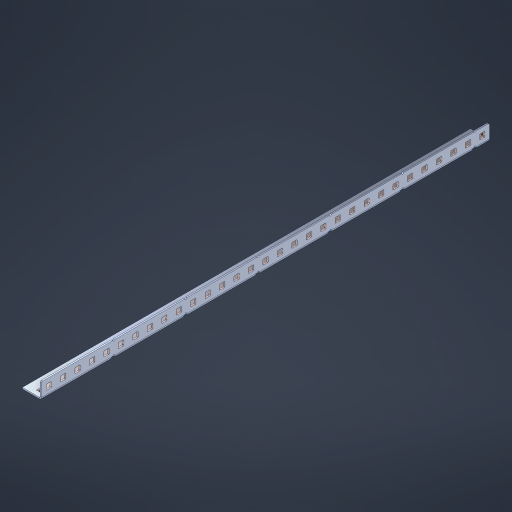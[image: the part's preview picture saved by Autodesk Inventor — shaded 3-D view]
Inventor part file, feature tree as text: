
AUTODESK INVENTOR PART (.ipt)
format: ipt  version: 2023 (Build 270158000, 158)  size: 975,872 bytes
history: native  units: in
note: dims shown in document units (in); Inventor stores cm internally (conversion verified against a paired STEP export)
features: other x67, extrude x61, sheet_metal_op x10, sketch x8, mirror x1, pattern_linear x1, chamfer x1
ambient origin geometry x8: Origin, YZ Plane, XZ Plane, XY Plane, X Axis, Y Axis, Z Axis, Center Point
bodies: Solid1 (feature_tree), Body (feature_tree)
feature tree (149):
  other  "Flange Pattern Plane"
  sheet_metal_op  "Flange Pattern"
  sheet_metal_op  "Body Pattern"
  other  "Arc Length"
  mirror  "Notch Mirror"
  pattern_linear  "Notch Pattern"  Spacing1=0.1875in  [1 undecoded]
  chamfer  "End Chamfer"
  extrude  "Half Cut"  Depth=0.0469in
  sketch  "Sketch1"  dims[d0=2.5in]
  other  "Plate1"
  sketch  "Sketch2"  dims[d1=15.5in]
  other  "Plate2"
  sheet_metal_op  "Bend1"
  sheet_metal_op  "Corner1"
  sketch  "Sketch3"  dims[d2=0.0469in]
  other  "Flange Pattern Sketch"
  sketch  "Sketch7"  dims[d3=0.0469in]
  other  "Srf1"
  other  "Srf2"
  sketch  "Sketch8"  dims[d4=0.0234in]
  sketch  "Sketch9"  dims[d5=0.0938in]
  other  "Srf91"
  sheet_metal_op  "Body Pattern Sketch"
  other  "Srf92"
  sketch  "Sketch13"  dims[d6=0.0469in]
  sketch  "Sketch14"  dims[d7=0.5in d8=90.0deg d9=0.0312in d10=0.1875in d11=0.0469in d12=0.0469in d16=0.182in d17=0.02in d18=0.0469in d19=0.0in d20=0.25in d21=0.25in d46=0.172in d47=1.0in d48=0.0in d49=0.182in d50=0.02in d51=0.25in d52=0.25in d53=0.0469in d54=0.0in d55=0.172in d56=1.0in d57=0.0in d60=12.2047in d62=0.5in d63=0.3937in d65=0.5in d85=0.1227in d86=0.1659in d88=0.04in d89=0.0469in d90=0.0in d91=0.04in d92=0.0491in d95=2.5in d96=0.04in d97=0.25in d98=45.0deg d101=0.0in d102=2.497in d131=0.5in d132=12.2047in d134=0.5in d139=0.5in]
  other  "Srf856"
  other  "Srf1310"
  other  "Srf1311"
  other  "Srf1312"
  other  "Srf1376"
  other  "Srf1377"
  other  "Srf1728"
  other  "Srf1755"
  other  "Srf1878"
  other  "Srf1879"
  other  "Srf1880"
  other  "Srf1881"
  other  "Srf1882"
  other  "Srf1883"
  other  "Srf1884"
  other  "Srf1885"
  other  "Srf1886"
  other  "Srf1887"
  other  "Srf1888"
  other  "Srf1889"
  other  "Srf1890"
  other  "Srf1891"
  other  "Srf1892"
  other  "Srf1893"
  other  "Srf1894"
  other  "Srf1895"
  other  "Srf1896"
  other  "Srf1897"
  other  "Srf1898"
  other  "Srf1899"
  other  "Srf1900"
  other  "Srf1901"
  other  "Srf1902"
  other  "Srf1942"
  other  "Srf1943"
  other  "Srf1944"
  other  "Srf1945"
  other  "Srf1946"
  other  "Srf1947"
  other  "Srf1948"
  other  "Srf1949"
  other  "Srf1950"
  other  "Srf1951"
  other  "Srf1952"
  other  "Srf1953"
  other  "Srf1954"
  other  "Srf1955"
  other  "Srf1956"
  other  "Srf1957"
  other  "Srf1958"
  other  "Srf1959"
  other  "Srf1960"
  other  "Srf1961"
  other  "Srf1962"
  other  "Srf1963"
  other  "Srf1964"
  other  "Srf1965"
  other  "Srf1966"
  sheet_metal_op  "Flange Stamp"
  sheet_metal_op  "Flange Circle"
  sheet_metal_op  "Body Stamp"
  sheet_metal_op  "Body Circle"
  sheet_metal_op  "Notch"
  extrude  "ExtrusionSrf2"  Depth=0.0469in
  extrude  "ExtrusionSrf92"  Depth=0.5in
  extrude  "ExtrusionSrf856"  Depth=0.02in
  extrude  "ExtrusionSrf1310"  Depth=0.0469in
  extrude  "ExtrusionSrf1311"  TaperAngle=0.0deg  [1 undecoded]
  extrude  "ExtrusionSrf1312"  Depth=0.5in
  extrude  "ExtrusionSrf1376"  Depth=0.5in
  extrude  "ExtrusionSrf1377"  Depth=0.5in
  extrude  "ExtrusionSrf1728"  Depth=0.5in TaperAngle=0.0deg
  extrude  "ExtrusionSrf1755"  Depth=0.5in
  extrude  "ExtrusionSrf1878"  Depth=0.02in
  extrude  "ExtrusionSrf1879"  Depth=0.5in
  extrude  "ExtrusionSrf1880"  Depth=0.5in
  extrude  "ExtrusionSrf1881"  Depth=0.0469in
  extrude  "ExtrusionSrf1882"  TaperAngle=0.0deg  [1 undecoded]
  extrude  "ExtrusionSrf1883"  Depth=0.5in
  extrude  "ExtrusionSrf1884"  Depth=0.5in TaperAngle=0.0deg
  extrude  "ExtrusionSrf1885"  Depth=0.5in
  extrude  "ExtrusionSrf1886"  Depth=0.5in
  extrude  "ExtrusionSrf1887"  Depth=0.5in
  extrude  "ExtrusionSrf1888"  Depth=0.5in
  extrude  "ExtrusionSrf1889"  Depth=0.5in
  extrude  "ExtrusionSrf1890"  Depth=0.0469in
  extrude  "ExtrusionSrf1891"  TaperAngle=0.0deg  [1 undecoded]
  extrude  "ExtrusionSrf1892"  Depth=0.5in
  extrude  "ExtrusionSrf1893"  Depth=0.5in
  extrude  "ExtrusionSrf1894"  Depth=0.5in
  extrude  "ExtrusionSrf1895"  Depth=0.5in TaperAngle=45.0deg
  extrude  "ExtrusionSrf1896"  TaperAngle=0.0deg  [1 undecoded]
  extrude  "ExtrusionSrf1897"  Depth=0.5in
  extrude  "ExtrusionSrf1898"  Depth=0.5in
  extrude  "ExtrusionSrf1899"  Depth=0.5in
  extrude  "ExtrusionSrf1900"  Depth=0.5in
  extrude  "ExtrusionSrf1901"  Depth=0.5in
  extrude  "ExtrusionSrf1902"  [1 undecoded]
  extrude  "ExtrusionSrf1942"  [1 undecoded]
  extrude  "ExtrusionSrf1943"  [1 undecoded]
  extrude  "ExtrusionSrf1944"  [1 undecoded]
  extrude  "ExtrusionSrf1945"  [1 undecoded]
  extrude  "ExtrusionSrf1946"  [1 undecoded]
  extrude  "ExtrusionSrf1947"  [1 undecoded]
  extrude  "ExtrusionSrf1948"  [1 undecoded]
  extrude  "ExtrusionSrf1949"  [1 undecoded]
  extrude  "ExtrusionSrf1950"  [1 undecoded]
  extrude  "ExtrusionSrf1951"  [1 undecoded]
  extrude  "ExtrusionSrf1952"  [1 undecoded]
  extrude  "ExtrusionSrf1953"  [1 undecoded]
  extrude  "ExtrusionSrf1954"  [1 undecoded]
  extrude  "ExtrusionSrf1955"  [1 undecoded]
  extrude  "ExtrusionSrf1956"  [1 undecoded]
  extrude  "ExtrusionSrf1957"  [1 undecoded]
  extrude  "ExtrusionSrf1958"  [1 undecoded]
  extrude  "ExtrusionSrf1959"  [1 undecoded]
  extrude  "ExtrusionSrf1960"  [1 undecoded]
  extrude  "ExtrusionSrf1961"  [1 undecoded]
  extrude  "ExtrusionSrf1962"  [1 undecoded]
  extrude  "ExtrusionSrf1963"  [1 undecoded]
  extrude  "ExtrusionSrf1964"  [1 undecoded]
  extrude  "ExtrusionSrf1965"  [1 undecoded]
  extrude  "ExtrusionSrf1966"  [1 undecoded]
note: 31 required parameter values undecoded (feature->parameter linkage not recoverable at this tier; creation-order binding heuristic only, values carry confidence <= 0.55)
